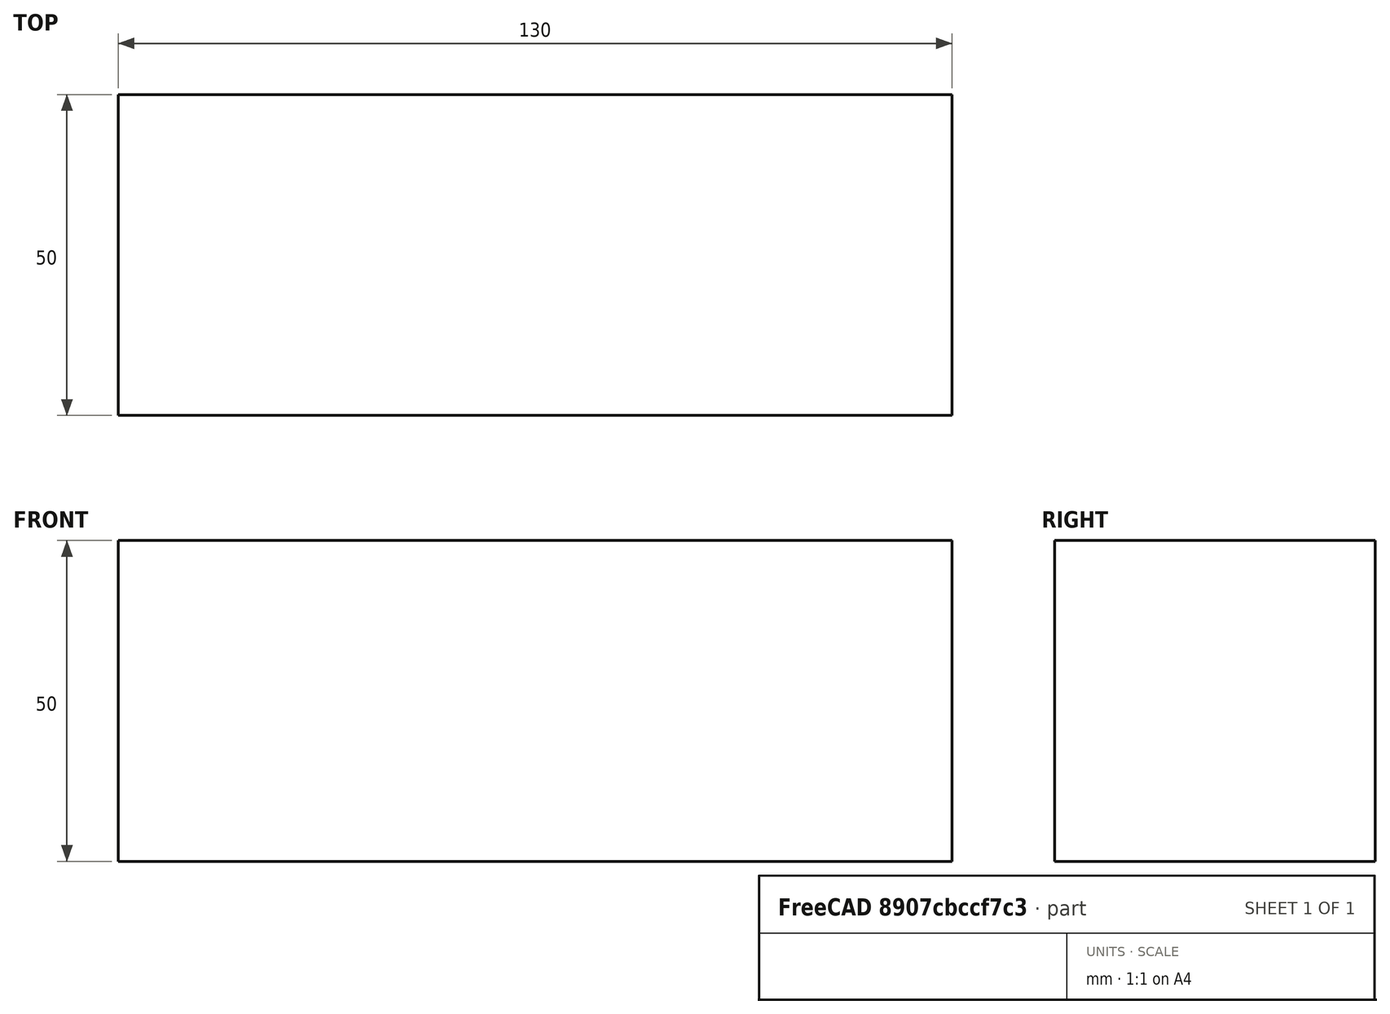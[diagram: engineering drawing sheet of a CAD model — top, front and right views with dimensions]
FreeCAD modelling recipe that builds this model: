
FCSTD DOCUMENT  (FreeCAD 0.15R4671 (Git))
Label: Flat Bar 130x50 EN10058 S235JR
License: All rights reserved
LicenseURL: http://en.wikipedia.org/wiki/All_rights_reserved
objects: Sketcher::SketchObject×1, Part::Extrusion×1
note: 2 computed .brp shape members not serialized (recipe doc carries the construction recipe); baked Part::Feature solids carry a one-line shape summary decoded from their .brp

FEATURE [Sketcher::SketchObject] Sketch
  sketch-geometry (4):
    g0: LineSegment StartX=-65 StartY=-25 StartZ=0 EndX=65 EndY=-25 EndZ=0
    g1: LineSegment StartX=65 StartY=-25 StartZ=0 EndX=65 EndY=25 EndZ=0
    g2: LineSegment StartX=65 StartY=25 StartZ=0 EndX=-65 EndY=25 EndZ=0
    g3: LineSegment StartX=-65 StartY=25 StartZ=0 EndX=-65 EndY=-25 EndZ=0
  constraints (12):
    c: Coincident(g0,g1)
    c: Coincident(g1,g2)
    c: Coincident(g2,g3)
    c: Coincident(g3,g0)
    c: Horizontal(g0)
    c: Horizontal(g2)
    c: Vertical(g1)
    c: Vertical(g3)
    c: Symmetric(g1,g2,g-2)
    c: Symmetric(g0,g1,g-1)
    c: DistanceY(g1) = 50
    c: DistanceX(g0) = 130
FEATURE [Part::Extrusion] Extrude  label="Flat Bar 130x50 EN10058 S235JR"
  Base = -> Sketch
  Dir = (0,0,50)
  Solid = true
